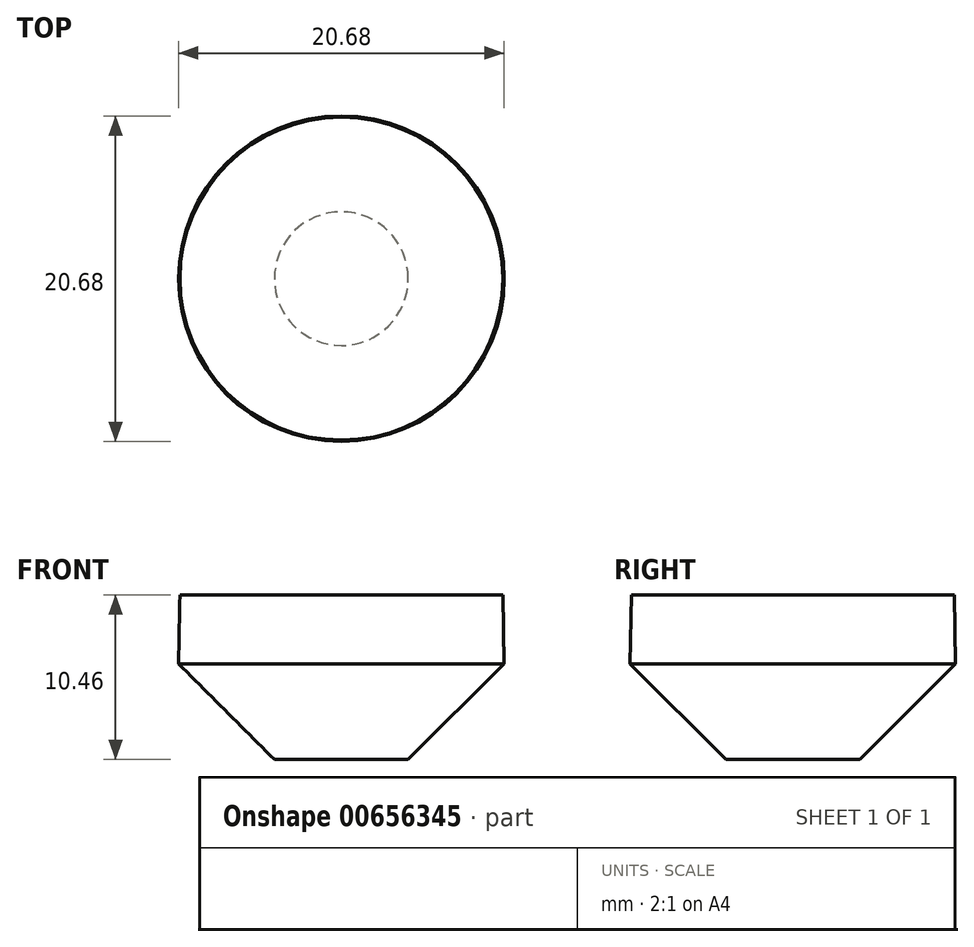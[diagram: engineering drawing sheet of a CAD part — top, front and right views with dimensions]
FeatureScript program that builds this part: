
annotation { "Feature Type Name" : "Feature", "Feature Type Description" : "" }
export const myFeature = defineFeature(function(context is Context, id is Id, definition is map)
    precondition{}
    {
        {
            var Q0;
            Q0=qCreatedBy(makeId("Front.planeOp"),FACE);
            var sketch = newSketch(context, id + "F0", { "sketchPlane" : qUnion([Q0])});
            skLineSegment(sketch, "E0.4", {"start": v(0, -10.58) * mm, "end": v(-4.25, -10.58) * mm});
            skLineSegment(sketch, "E0.5", {"start": v(-4.25, -10.58) * mm, "end": v(-10.34, -4.49) * mm});
            skLineSegment(sketch, "E0.6", {"start": v(-10.34, -4.49) * mm, "end": v(-10.25, -0.12) * mm});
            skLineSegment(sketch, "E1", {"start": v(-10.25, -0.12) * mm, "end": v(0, -0.12) * mm});
            skPoint(sketch, "E2.orphan", {"position": v(0, 8.63) * mm});
            skLineSegment(sketch, "E3", {"start": v(0, -0.12) * mm, "end": v(0, -10.58) * mm});
            skSolve(sketch);
        }
        {
            var Q0;
            Q0=sQuery(id+"F0.wireOp",EDGE,"E1");
            var Q1;
            Q1=sQuery(id+"F0.wireOp",EDGE,"E0.6");
            var Q2;
            Q2=sQuery(id+"F0.wireOp",EDGE,"E0.5");
            var Q3;
            Q3=sQuery(id+"F0.wireOp",EDGE,"E0.4");
            var Q4;
            Q4=sQuery(id+"F0.wireOp",EDGE,"E3");
            revolve(context, id + "F1", {"bodyType" : ToolBodyType.SURFACE, "surfaceEntities" : qUnion([Q0, Q1, Q2, Q3]), "axis" : qUnion([Q4]), "revolveType" : RevolveType.FULL});
        }
    });
